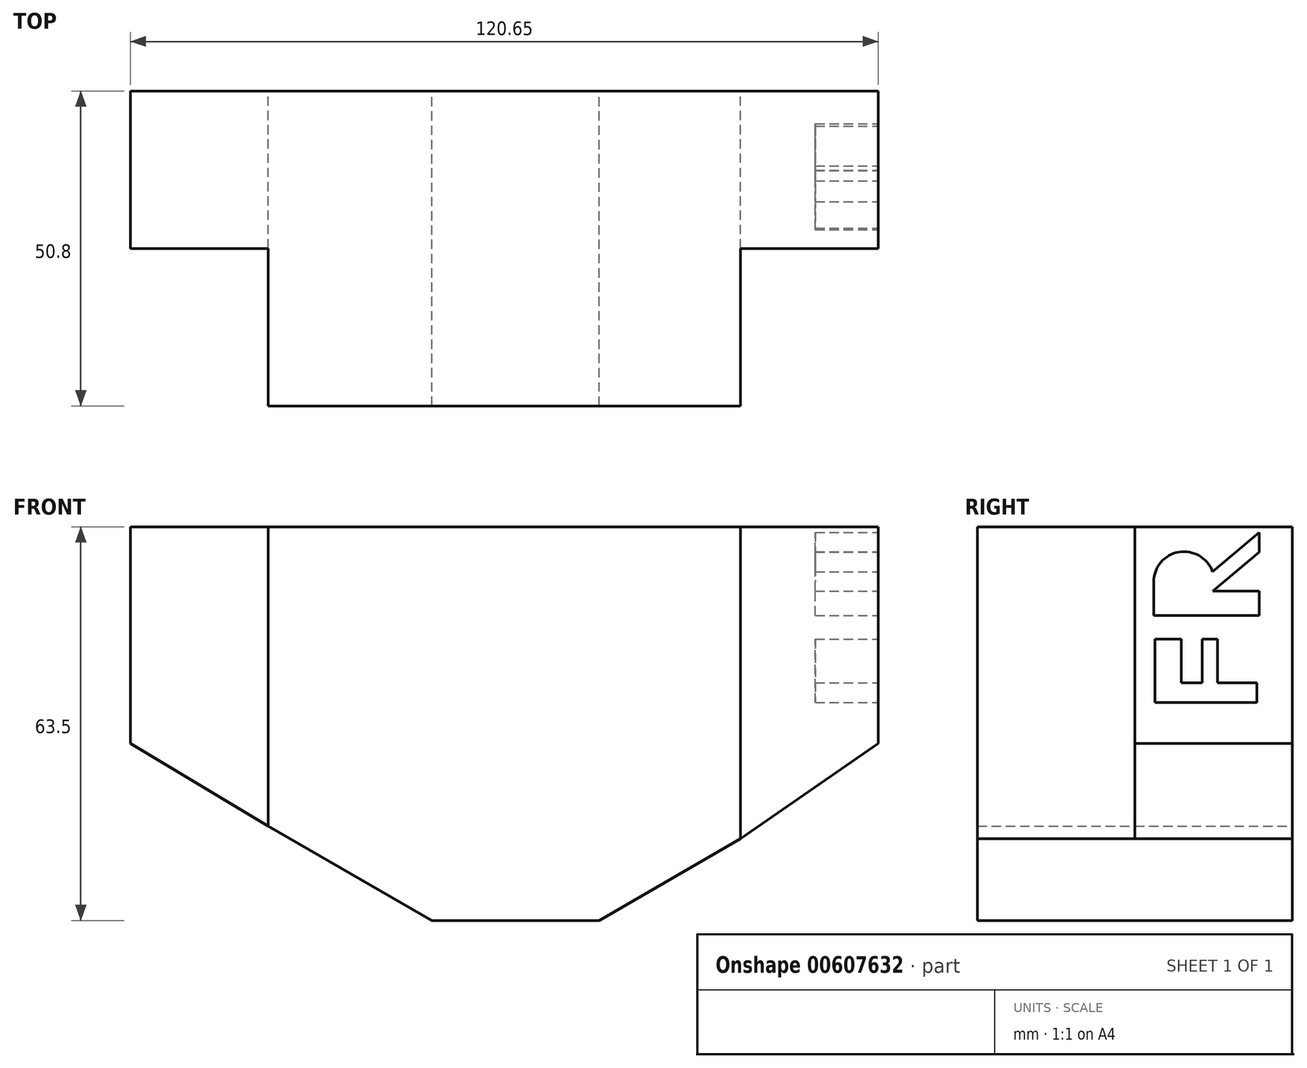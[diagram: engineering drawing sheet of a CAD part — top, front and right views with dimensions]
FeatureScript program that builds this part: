
annotation { "Feature Type Name" : "Feature", "Feature Type Description" : "" }
export const myFeature = defineFeature(function(context is Context, id is Id, definition is map)
    precondition{}
    {
        {
            var Q0;
            Q0=qCreatedBy(makeId("Front.planeOp"),FACE);
            var sketch = newSketch(context, id + "F0", { "sketchPlane" : qUnion([Q0])});
            skLineSegment(sketch, "E0.bottom", {"start": v(-45.05, 0) * mm, "end": v(-72.04, 0) * mm});
            skLineSegment(sketch, "E0.top", {"start": v(0, 63.5) * mm, "end": v(-120.65, 63.5) * mm});
            skLineSegment(sketch, "E0.left", {"start": v(0, 28.58) * mm, "end": v(0, 63.5) * mm});
            skLineSegment(sketch, "E0.right", {"start": v(-120.65, 28.57) * mm, "end": v(-120.65, 63.5) * mm});
            skLineSegment(sketch, "E1", {"start": v(-72.04, 0) * mm, "end": v(-45.05, 0) * mm});
            skLineSegment(sketch, "E2", {"start": v(-72.04, 0) * mm, "end": v(-98.43, 15.24) * mm});
            skLineSegment(sketch, "E3", {"start": v(-98.43, 15.24) * mm, "end": v(-120.65, 28.57) * mm});
            skLineSegment(sketch, "E4", {"start": v(-45.05, 0) * mm, "end": v(-22.23, 13.18) * mm});
            skLineSegment(sketch, "E5", {"start": v(-22.23, 13.18) * mm, "end": v(0, 28.58) * mm});
            skSolve(sketch);
        }
        {
            var Q0;
            Q0=makeQuery(id+"F0.imprint","IMPRINT",FACE,{"disambiguationData":[TD([[makeQuery(id+"F0.imprint","IMPRINT",EDGE,{"derivedFrom":sQuery(id+"F0.wireOp",EDGE,"E0.top")}),1.0]])]});
            extrude(context, id + "F1", {"entities" : qUnion([Q0]), "depth" : 50.8 * mm, "offsetDistance" : 25.4 * mm});
        }
        {
            var Q0;
            Q0=makeQuery(id+"F1.opExtrude","CAP_FACE",FACE,{"disambiguationData":[OSD([sQuery(id+"F0.wireOp",EDGE,"E0.top"),sQuery(id+"F0.wireOp",EDGE,"E0.left"),sQuery(id+"F0.wireOp",EDGE,"E0.right"),sQuery(id+"F0.wireOp",EDGE,"E1"),sQuery(id+"F0.wireOp",EDGE,"E2"),sQuery(id+"F0.wireOp",EDGE,"E3"),sQuery(id+"F0.wireOp",EDGE,"E4"),sQuery(id+"F0.wireOp",EDGE,"E5")])],"isStart":false});
            var sketch = newSketch(context, id + "F2", { "sketchPlane" : qUnion([Q0])});
            skLineSegment(sketch, "E6", {"start": v(-22.23, 13.18) * mm, "end": v(-22.23, 63.5) * mm});
            skLineSegment(sketch, "E7", {"start": v(-98.43, 15.24) * mm, "end": v(-98.43, 63.5) * mm});
            skSolve(sketch);
        }
        {
            var Q0;
            {var subQ0=sQuery(id+"F2.wireOp",EDGE,"E6");Q0=makeQuery(id+"F2.imprint","IMPRINT",FACE,{"disambiguationData":[TD([[makeQuery(id+"F2.imprint","IMPRINT",EDGE,{"derivedFrom":subQ0}),-1.0]])]});}
            var Q1;
            {var subQ0=sQuery(id+"F2.wireOp",EDGE,"E7");Q1=makeQuery(id+"F2.imprint","IMPRINT",FACE,{"disambiguationData":[TD([[makeQuery(id+"F2.imprint","IMPRINT",EDGE,{"derivedFrom":subQ0}),1.0]])]});}
            extrude(context, id + "F3", {"entities" : qUnion([Q0, Q1]), "operationType" : NewBodyOperationType.REMOVE, "oppositeDirection" : true, "depth" : 25.4 * mm, "offsetDistance" : 25.4 * mm});
        }
        {
            var Q0;
            Q0=makeQuery(id+"F1.opExtrude","SWEPT_FACE",FACE,{"disambiguationData":[OSD([sQuery(id+"F0.wireOp",EDGE,"E0.left")])]});
            var sketch = newSketch(context, id + "F4", { "sketchPlane" : qUnion([Q0])});
            skLineSegment(sketch, "E8", {"start": v(-5.4, 35.17) * mm, "end": v(-22.14, 35.17) * mm});
            skLineSegment(sketch, "E9", {"start": v(-22.14, 35.17) * mm, "end": v(-22.14, 45.37) * mm});
            skLineSegment(sketch, "E10", {"start": v(-22.14, 45.37) * mm, "end": v(-17.88, 45.37) * mm});
            skLineSegment(sketch, "E11", {"start": v(-17.88, 45.37) * mm, "end": v(-17.88, 38.36) * mm});
            skLineSegment(sketch, "E12", {"start": v(-17.88, 38.36) * mm, "end": v(-14.52, 38.36) * mm});
            skLineSegment(sketch, "E13", {"start": v(-14.52, 38.36) * mm, "end": v(-14.52, 45.37) * mm});
            skLineSegment(sketch, "E14", {"start": v(-14.52, 45.37) * mm, "end": v(-12.09, 45.37) * mm});
            skLineSegment(sketch, "E15", {"start": v(-12.09, 45.37) * mm, "end": v(-12.09, 38.36) * mm});
            skLineSegment(sketch, "E16", {"start": v(-12.09, 38.36) * mm, "end": v(-5.68, 38.36) * mm});
            skLineSegment(sketch, "E17", {"start": v(-5.68, 38.36) * mm, "end": v(-5.68, 35.17) * mm});
            skLineSegment(sketch, "E18", {"start": v(-22.35, 49.19) * mm, "end": v(-5.3, 49.19) * mm});
            skLineSegment(sketch, "E19", {"start": v(-5.3, 49.19) * mm, "end": v(-5.3, 53.15) * mm});
            skLineSegment(sketch, "E20", {"start": v(-5.3, 53.15) * mm, "end": v(-12.81, 53.15) * mm});
            skLineSegment(sketch, "E21", {"start": v(-12.81, 53.15) * mm, "end": v(-5.3, 59.42) * mm});
            skLineSegment(sketch, "E22", {"start": v(-5.3, 59.42) * mm, "end": v(-5.3, 62.56) * mm});
            skLineSegment(sketch, "E23", {"start": v(-5.3, 62.56) * mm, "end": v(-12.87, 56.24) * mm});
            skLineSegment(sketch, "E24", {"start": v(-22.35, 49.19) * mm, "end": v(-22.35, 54.6) * mm});
            skArc(sketch, "E25", {"start": v(-12.87, 56.24) * mm, "mid": v(-18.3, 59.42) * mm, "end": v(-22.35, 54.6) * mm});
            skLineSegment(sketch, "E26", {"start": v(-19.99, 53.03) * mm, "end": v(-15.28, 53.03) * mm});
            skLineSegment(sketch, "E27", {"start": v(-15.28, 53.03) * mm, "end": v(-15.28, 54.6) * mm});
            skLineSegment(sketch, "E28", {"start": v(-15.28, 54.6) * mm, "end": v(-20.1, 54.6) * mm});
            skLineSegment(sketch, "E29", {"start": v(-20.1, 54.6) * mm, "end": v(-20.1, 53.15) * mm});
            skSolve(sketch);
        }
        {
            var Q0;
            {var subQ0=sQuery(id+"F4.wireOp",EDGE,"E9");Q0=makeQuery(id+"F4.imprint","IMPRINT",FACE,{"disambiguationData":[TD([[makeQuery(id+"F4.imprint","IMPRINT",EDGE,{"derivedFrom":subQ0}),-1.0]])]});}
            var Q1;
            Q1=makeQuery(id+"F4.imprint","IMPRINT",FACE,{"disambiguationData":[TD([[makeQuery(id+"F4.imprint","IMPRINT",EDGE,{"derivedFrom":sQuery(id+"F4.wireOp",EDGE,"E18")}),1.0]])]});
            extrude(context, id + "F5", {"entities" : qUnion([Q0, Q1]), "operationType" : NewBodyOperationType.REMOVE, "oppositeDirection" : true, "depth" : 10.16 * mm, "offsetDistance" : 25.4 * mm});
        }
    });
